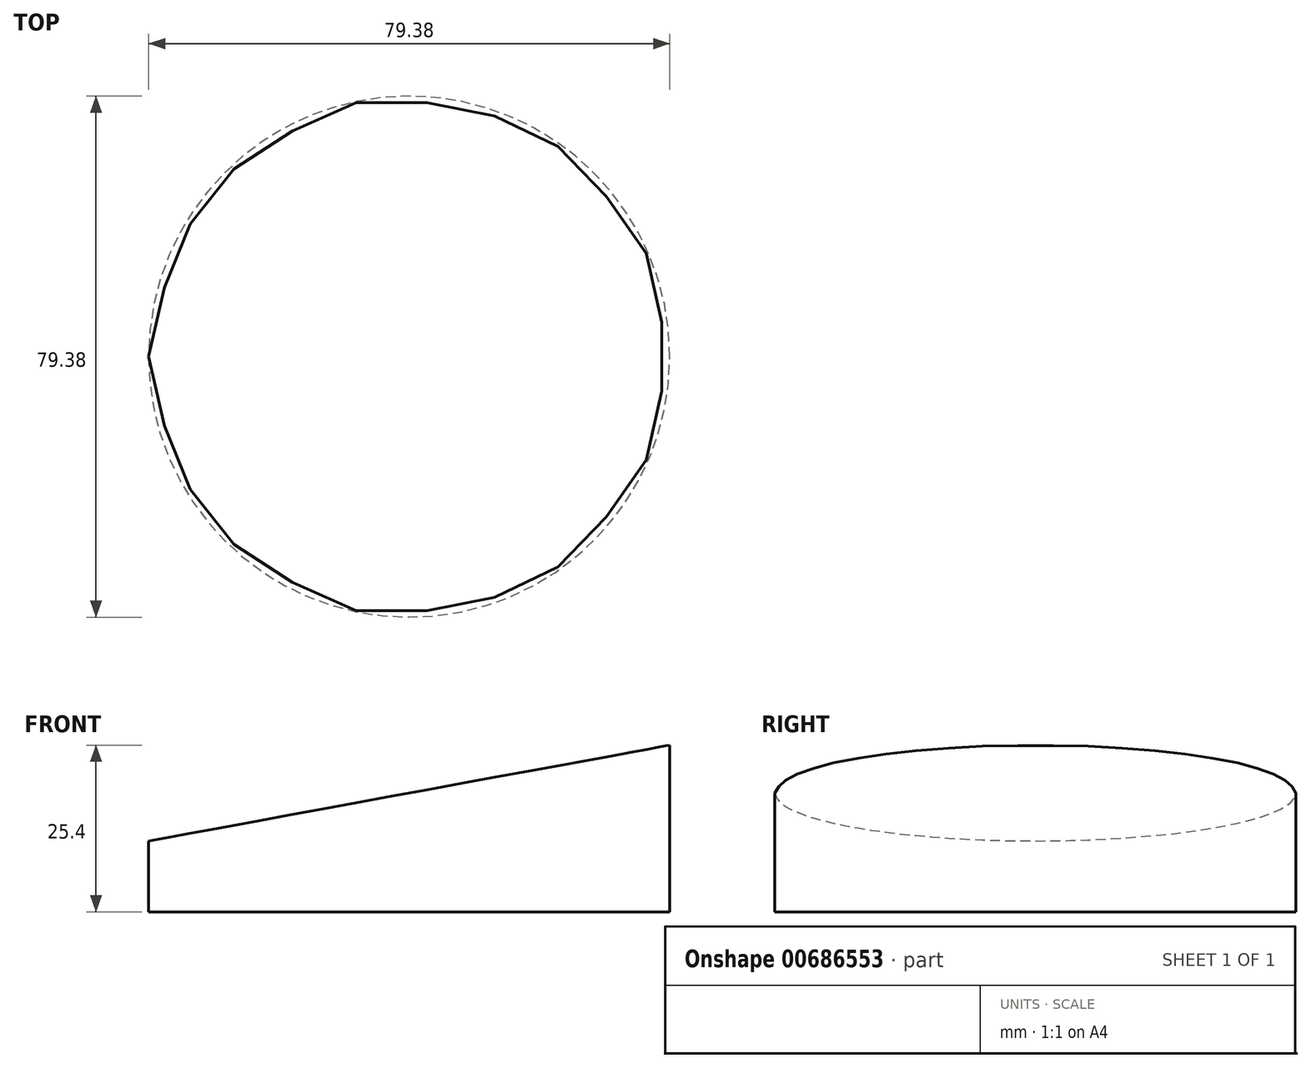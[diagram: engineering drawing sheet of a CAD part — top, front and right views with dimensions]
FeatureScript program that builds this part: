
annotation { "Feature Type Name" : "Feature", "Feature Type Description" : "" }
export const myFeature = defineFeature(function(context is Context, id is Id, definition is map)
    precondition{}
    {
        {
            var Q0;
            Q0=qCreatedBy(makeId("Top.planeOp"),FACE);
            var sketch = newSketch(context, id + "F0", { "sketchPlane" : qUnion([Q0])});
            skCircle(sketch, "E0", {"center": v(0, 0) * mm, "radius": 39.69 * mm});
            skSolve(sketch);
        }
        {
            var Q0;
            Q0 = qSketchRegion(id + "F0", true);
            var Q1;
            Q1=makeQuery(id+"F0.imprint","IMPRINT",FACE,{"disambiguationData":[TD([[makeQuery(id+"F0.imprint","IMPRINT",EDGE,{"derivedFrom":sQuery(id+"F0.wireOp",EDGE,"E0")}),1.0]])]});
            extrude(context, id + "F1", {"entities" : qUnion([Q0, Q1]), "depth" : 25.4 * mm, "offsetDistance" : 25.4 * mm});
        }
        {
            var Q0;
            Q0=qCreatedBy(makeId("Front.planeOp"),FACE);
            var sketch = newSketch(context, id + "F2", { "sketchPlane" : qUnion([Q0])});
            skLineSegment(sketch, "E1", {"start": v(39.8, 25.42) * mm, "end": v(-46.4, 9.57) * mm});
            skLineSegment(sketch, "E2", {"start": v(-46.4, 9.57) * mm, "end": v(-46.4, 31.82) * mm});
            skLineSegment(sketch, "E3", {"start": v(-46.4, 31.82) * mm, "end": v(39.8, 25.42) * mm});
            skSolve(sketch);
        }
        {
            var Q0;
            Q0=makeQuery(id+"F2.imprint","IMPRINT",FACE,{"disambiguationData":[TD([[makeQuery(id+"F2.imprint","IMPRINT",EDGE,{"derivedFrom":sQuery(id+"F2.wireOp",EDGE,"E1")}),-1.0]])]});
            extrude(context, id + "F3", {"entities" : qUnion([Q0]), "operationType" : NewBodyOperationType.REMOVE, "endBound" : BoundingType.THROUGH_ALL, "depth" : 25.4 * mm, "offsetDistance" : 25.4 * mm, "hasSecondDirection" : true, "secondDirectionBound" : SecondDirectionBoundingType.THROUGH_ALL, "secondDirectionOppositeDirection" : true, "secondDirectionDepth" : 25.4 * mm});
        }
    });
